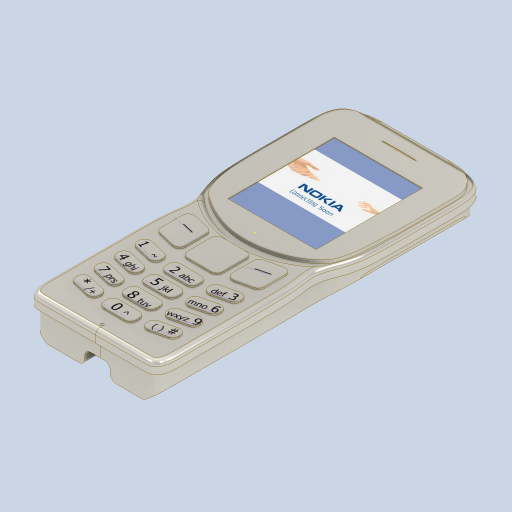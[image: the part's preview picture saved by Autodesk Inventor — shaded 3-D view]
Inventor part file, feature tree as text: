
AUTODESK INVENTOR PART (.ipt)
format: ipt  version: 2024 (Build 280153020, 153B)  size: 1,211,904 bytes
history: native  units: in
note: dims shown in document units (in); Inventor stores cm internally (conversion verified against a paired STEP export)
features: sketch x18, extrude x15, other x8, fillet x8, plane x6, projected_geometry x3, delete_face x2, hole x1
ambient origin geometry x8: Origin, YZ Plane, XZ Plane, XY Plane, X Axis, Y Axis, Z Axis, Center Point
bodies: Body1 (feature_tree)
feature tree (61):
  other  "Nokia3310.ipt"
  plane  "Work Plane1"
  extrude  "Extrusion1"  Depth=0.3937in
  extrude  "Extrusion2"  Depth=0.3937in
  extrude  "Extrusion4"  Depth=0.3937in
  extrude  "Extrusion5"  Depth=1.2675in
  extrude  "Extrusion6"  Depth=0.2362in TaperAngle=0.0deg
  fillet  "Fillet1"  Radius=0.0276in
  extrude  "Extrusion7"  Depth=0.1969in TaperAngle=0.0deg
  fillet  "Fillet2"  Radius=0.0787in
  extrude  "Extrusion8"  Depth=0.2362in TaperAngle=0.0deg
  hole  "Hole1"  [1 undecoded]
  extrude  "Extrusion9"  Depth=0.0787in
  plane  "Work Plane3"
  extrude  "Extrusion10"  Depth=0.962in
  delete_face  "Delete Face1"
  fillet  "Fillet3"  Radius=0.0763in
  fillet  "Fillet4"  Radius=0.0787in
  fillet  "Fillet5"  Radius=0.0787in
  plane  "Work Plane5"
  extrude  "Extrusion11"  Depth=0.0197in TaperAngle=0.0deg
  delete_face  "Delete Face2"
  fillet  "Fillet7"  Radius=0.1575in
  fillet  "Fillet8"  Radius=0.0433in
  extrude  "Extrusion12"  Depth=0.0197in TaperAngle=0.0deg
  extrude  "Extrusion13"  [1 undecoded]
  fillet  "Fillet9"  [1 undecoded]
  sketch  "Sketch21"
  plane  "Work Plane7"
  extrude  "Extrusion15"  [1 undecoded]
  extrude  "Extrusion16"  [1 undecoded]
  extrude  "Extrusion17"  [1 undecoded]
  other  "Decal1"
  other  "Top::Nokia3310.ipt"
  other  "TaggingFeature1"
  sketch  "Sketch2"  dims[d0=0.3937in d2=0.0787in]
  sketch  "Sketch3"  dims[d3=0.3937in d4=0.0in d5=0.0591in]
  projected_geometry  "Projected Loop2"
  sketch  "Sketch5"  dims[d6=0.3937in d7=0.0in d15=0.6693in]
  sketch  "Sketch6"  dims[d16=2.0866in d17=1.2675in]
  sketch  "Sketch7"  dims[d18=0.2362in d19=0.0in d20=0.2362in d21=0.0in d22=0.0276in d23=0.0in]
  sketch  "Sketch8"  dims[d24=0.0787in d25=0.1969in d26=0.0in d27=0.0787in]
  sketch  "Sketch9"  dims[d28=0.2362in d29=0.0in]
  sketch  "Sketch10"  dims[d30=0.1575in d31=0.2362in d32=0.1575in d33=0.0787in d34=90.0deg d35=0.7874in d36=0.8108in d37=0.2362in d38=0.0in]
  sketch  "Sketch11"  dims[d39=0.962in d40=-0.2756in d42=0.0763in d43=0.0in]
  plane  "Work Plane2"
  sketch  "Sketch13"  dims[d44=0.0787in d45=0.0787in]
  plane  "Work Plane4"
  sketch  "Sketch14"  dims[d46=0.0787in d47=0.962in d48=-0.0079in d49=0.0763in d50=0.0in d52=0.0787in d53=0.0787in]
  sketch  "Sketch15"  dims[d54=0.0197in d55=0.0in d56=0.0197in d57=0.0in d58=0.1575in d62=0.0433in d63=0.0in]
  sketch  "Sketch16"  dims[d64=0.0197in d65=0.0in d66=0.0197in d67=0.0in]
  sketch  "Sketch22"
  projected_geometry  "Projected Loop4"
  sketch  "Sketch23"
  sketch  "Sketch24"
  projected_geometry  "Projected Loop5"
  sketch  "Sketch25"
  other  "Image1"
  other  "Top"
  other  "Finish1"
  other  "Finish2"
note: 6 required parameter values undecoded (feature->parameter linkage not recoverable at this tier; creation-order binding heuristic only, values carry confidence <= 0.55)
